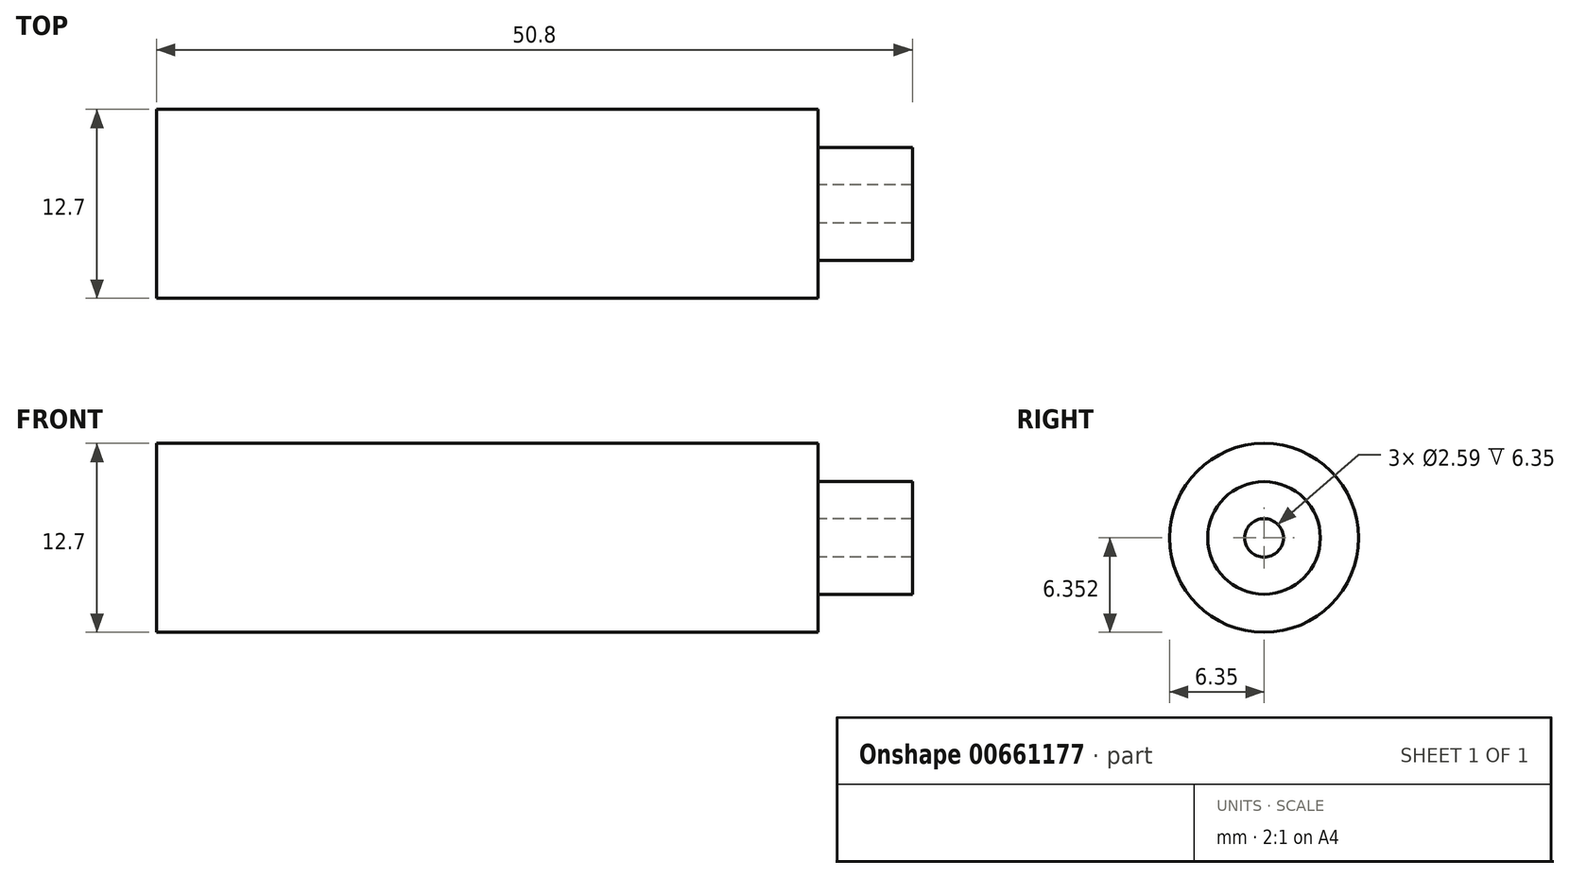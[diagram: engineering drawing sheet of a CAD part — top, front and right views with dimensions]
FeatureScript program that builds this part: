
annotation { "Feature Type Name" : "Feature", "Feature Type Description" : "" }
export const myFeature = defineFeature(function(context is Context, id is Id, definition is map)
    precondition{}
    {
        {
            var Q0;
            Q0=qCreatedBy(makeId("Front.planeOp"),FACE);
            var sketch = newSketch(context, id + "F0", { "sketchPlane" : qUnion([Q0])});
            skLineSegment(sketch, "E0.top", {"start": v(-67.55, 28.97) * mm, "end": v(-16.75, 28.97) * mm});
            skLineSegment(sketch, "E0.left", {"start": v(-67.55, 22.62) * mm, "end": v(-67.55, 28.97) * mm});
            skLineSegment(sketch, "E0.right", {"start": v(-16.75, 22.62) * mm, "end": v(-16.75, 28.97) * mm});
            skLineSegment(sketch, "E1", {"start": v(-23.1, 22.62) * mm, "end": v(-23.1, 28.97) * mm});
            skPoint(sketch, "E2", {"position": v(-23.1, 23.92) * mm});
            skPoint(sketch, "E3", {"position": v(-23.1, 26.4) * mm});
            skLineSegment(sketch, "E4", {"start": v(-25.64, 22.62) * mm, "end": v(-25.64, 28.97) * mm});
            skLineSegment(sketch, "E5", {"start": v(-28.18, 22.62) * mm, "end": v(-28.18, 28.97) * mm});
            skLineSegment(sketch, "E6.bottom", {"start": v(-28.18, 28.97) * mm, "end": v(-25.64, 28.97) * mm});
            skLineSegment(sketch, "E6.top", {"start": v(-28.18, 31.51) * mm, "end": v(-25.64, 31.51) * mm});
            skLineSegment(sketch, "E6.left", {"start": v(-28.18, 28.97) * mm, "end": v(-28.18, 31.51) * mm});
            skLineSegment(sketch, "E6.right", {"start": v(-25.64, 28.97) * mm, "end": v(-25.64, 31.51) * mm});
            skLineSegment(sketch, "E7", {"start": v(-67.55, 22.62) * mm, "end": v(-16.75, 22.62) * mm});
            skLineSegment(sketch, "E8", {"start": v(-23.1, 26.4) * mm, "end": v(-16.75, 26.4) * mm});
            skLineSegment(sketch, "E9", {"start": v(-23.1, 23.92) * mm, "end": v(-16.75, 23.92) * mm});
            skSolve(sketch);
        }
        {
            var Q0;
            {var subQ0=sQuery(id+"F0.wireOp",EDGE,"ec17c115-c327-438e-8c62-801040099b91");Q0=makeQuery(id+"F0.imprint","IMPRINT",FACE,{"disambiguationData":[TD([[makeQuery(id+"F0.imprint","IMPRINT",EDGE,{"derivedFrom":subQ0}),-1.0]])]});}
            var Q1;
            {var subQ6=sQuery(id+"F0.wireOp",EDGE,"E4");Q1=makeQuery(id+"F0.imprint","IMPRINT",FACE,{"disambiguationData":[TD([[makeQuery(id+"F0.imprint","IMPRINT",EDGE,{"derivedFrom":subQ6}),-1.0]])]});}
            var Q2;
            {var subQ0=sQuery(id+"F0.wireOp",EDGE,"E4");Q2=makeQuery(id+"F0.imprint","IMPRINT",FACE,{"disambiguationData":[TD([[makeQuery(id+"F0.imprint","IMPRINT",EDGE,{"derivedFrom":subQ0}),1.0]])]});}
            var Q3;
            Q3=makeQuery(id+"F0.imprint","IMPRINT",FACE,{"disambiguationData":[TD([[makeQuery(id+"F0.imprint","IMPRINT",EDGE,{"derivedFrom":sQuery(id+"F0.wireOp",EDGE,"E6.bottom")}),1.0]])]});
            var Q4;
            {var subQ0=sQuery(id+"F0.wireOp",EDGE,"E0.left");Q4=makeQuery(id+"F0.imprint","IMPRINT",FACE,{"disambiguationData":[TD([[makeQuery(id+"F0.imprint","IMPRINT",EDGE,{"derivedFrom":subQ0}),-1.0]])]});}
            var Q5;
            {var subQ0=sQuery(id+"F0.wireOp",EDGE,"E8");Q5=makeQuery(id+"F0.imprint","IMPRINT",FACE,{"disambiguationData":[TD([[makeQuery(id+"F0.imprint","IMPRINT",EDGE,{"derivedFrom":subQ0}),-1.0]])]});}
            var Q6;
            Q6=sQuery(id+"F0.wireOp",EDGE,"E7");
            revolve(context, id + "F1", {"entities" : qUnion([Q0, Q1, Q2, Q3, Q4, Q5]), "axis" : qUnion([Q6]), "revolveType" : RevolveType.FULL});
        }
    });
